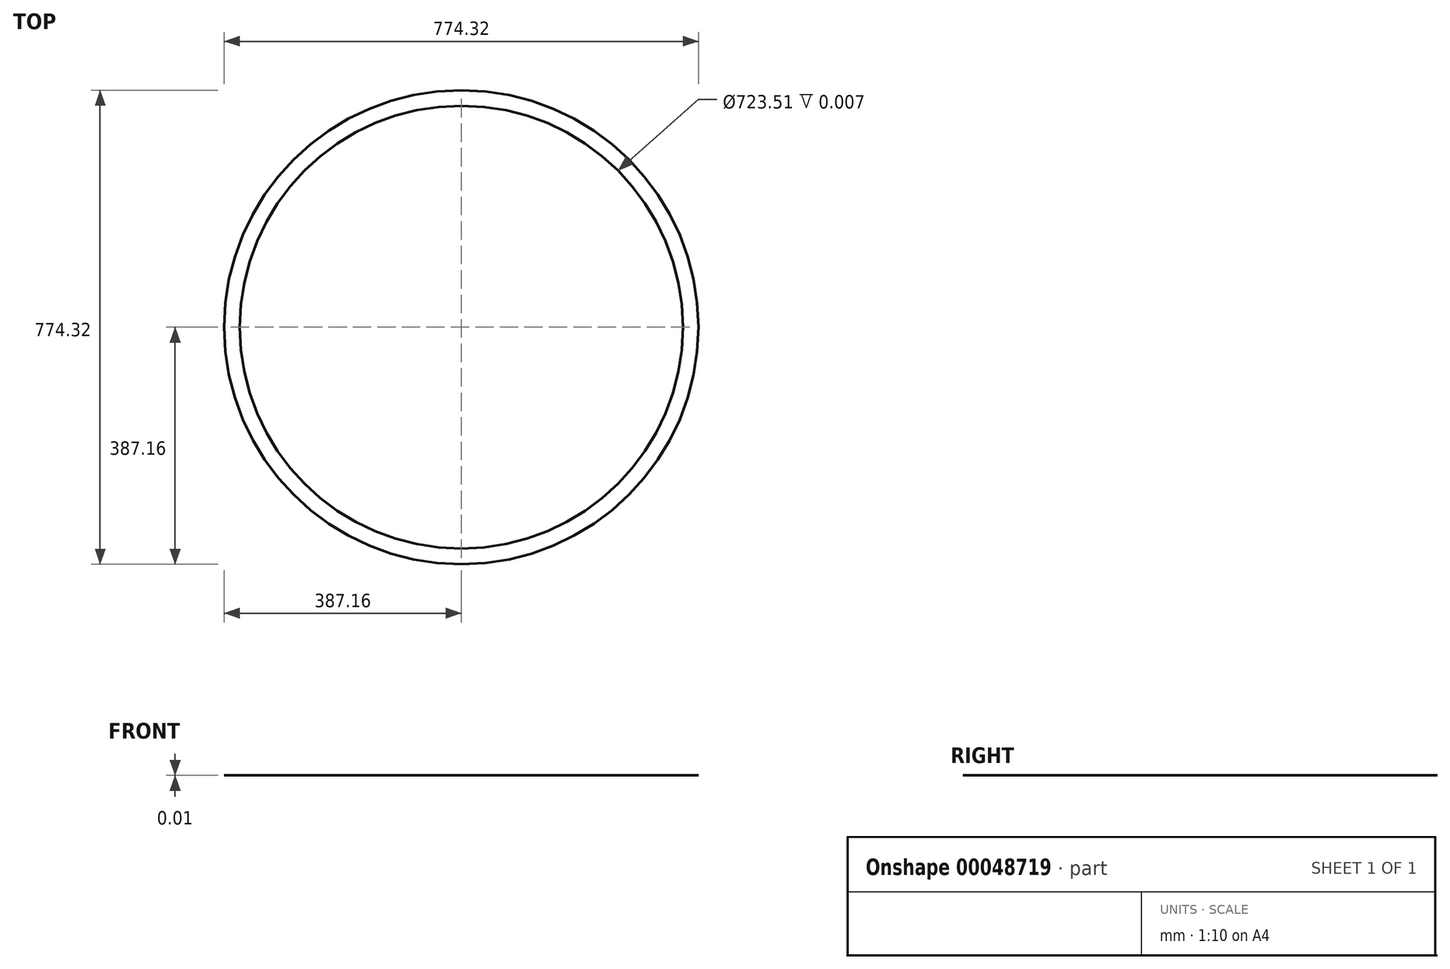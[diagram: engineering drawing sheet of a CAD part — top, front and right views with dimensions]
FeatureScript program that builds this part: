
annotation { "Feature Type Name" : "Feature", "Feature Type Description" : "" }
export const myFeature = defineFeature(function(context is Context, id is Id, definition is map)
    precondition{}
    {
        {
            var Q0;
            Q0=qCreatedBy(makeId("Top.planeOp"),FACE);
            var sketch = newSketch(context, id + "F0", { "sketchPlane" : qUnion([Q0])});
            skCircle(sketch, "E0", {"center": v(0, 0) * mm, "radius": 387.16 * mm});
            skCircle(sketch, "E1", {"center": v(0, 0) * mm, "radius": 361.76 * mm});
            skSolve(sketch);
        }
        {
            var Q0;
            Q0=makeQuery(id+"F0.imprint","IMPRINT",FACE,{"disambiguationData":[TD([[makeQuery(id+"F0.imprint","IMPRINT",EDGE,{"derivedFrom":sQuery(id+"F0.wireOp",EDGE,"E0")}),1.0]])]});
            extrude(context, id + "F1", {"entities" : qUnion([Q0]), "depth" : 3 / 406.4 * mm});
        }
    });
